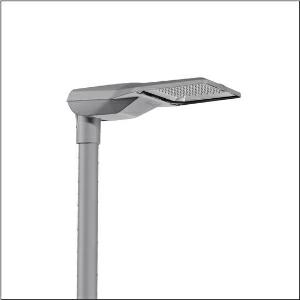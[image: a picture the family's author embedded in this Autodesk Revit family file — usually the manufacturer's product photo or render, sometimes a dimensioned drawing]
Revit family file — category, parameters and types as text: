
# Revit family: streetlight_sl_21_iq_midi___st0_8a_5xe3c61g08nb_b7e9
name_source: partatom
category: Lighting Fixtures
units: mm (PartAtom-declared; Revit-internal decimal feet)

## family parameters
Cut with Voids When Loaded = No
Host = Face
Light Source = No
Part Type = Normal
Room Calculation Point = No
Round Connector Dimension = Use Diameter
Shared = No

## types (1)
- --- (1 x LED, 20820 lm, 155.5 W, 2700K)
    Apparent Load = 155 VA
    CIE Flux Codes = 41 75 97 100 100
    Color Rendering = 70
    Color Temperature = 2700K
    Default Elevation = 1800 mm
    Description = Streetlight SL 21 iQ midi, mast luminaire, primary light control with lens, of PMMA, primary optical cover: cover, of toughened safety glass, transparent, light distribution: ST0.8a, light emission: direct distribution, primary light characteristic: asymmetric, installation type: post-top, side-entry, LED, High Power LED, rated luminous flux: 20.820lm, luminous efficacy: 134lm/W, light colour: 727, colour temperature: 2700K, control: Street-Remote, Auto-Match, Temp-Guard, Lumen-Switch, Night-Set, Smart-Wire, Light-Fading, Desk-Remote (wireless, voltage-free reading and setting of iQ features in the workshop via application-optimized NFC function/RFID function), optimised constant luminous flux control (CLO 2.0), presetting dimming linear, mains connection: 230..240V, AC, 50/60Hz, start of lifetime: 156W, end of service life: 162W, reduction: 69W, luminaire housing, of diecast aluminium, powder-coated, Siteco® metallic grey (DB 702S), corrosivity category C5 mid according to DIN EN ISO 12944, please order mast flange separately, inclination adjustable: 0°, 5°, 10°, 15°, sealing non-destructively replaceable, multi-level sealing system, length: 644mm, width: 335mm, height: 110mm, mast flange for spigot size: 42mm (side-entry): 5XC10008XM4, 60/48mm (side-entry/post-top): 5XC10108XM2, 76/60mm (side-entry/post-top): 5XC10108XM1, protection rating (complete): IP66, insulation class (complete): insulation class II (safety insulation), certification: CE, ENEC, ENEC+, VDE, impact resistance: IK09, permissible operating ambient temperature for outdoor applications: -40..+50°C, standard-compliant lighting for roads and squares, packaging unit: 1 piece

Light Distribution: ST0.8a
    Height = 111 mm
    Lamp = 1 x LED
    Lamp Light Flux = 20820 lm
    Lamp Power = 155.5 W
    Lamp count = 1
    Length = 644 mm
    Luminous efficacy = 134 lm/W
    Manufacturer = Siteco
    ModVariant = No
    Model = 5XE3C61G08NB
    Number of Poles = 1
    OnlyDefault = Yes
    Power Factor = 1
    Product Name = Streetlight SL 21 iQ midi | ST0.8a
    Product group = mast luminaire | pylon top
    ProductGroupID = 6100
    Protection Class = Protection class II
    Protection Degree = IP 66
    RLX_Detail_Level = 1
    RLX_Emergency_Light_Flux = 0 lm
    RLX_Emergency_Type = 0
    RLX_Emergency_Type_DB = No
    RlxData = <blob elided: 91277 chars, md5=0ad41ddc>
    Socket = socket
    Standby Power = 0 W
    System Light Flux = 20820 lm
    System Power = 155 W
    Type Comments = factory setting: luminous flux: 100 % | dim-lin: 254 | 823 mA
    Type Image = l_1004298.jpg
    URL = http://relux.com
    VarID = @adj_101225
    Voltage = 0 V
    Weight = 0.00 kg
    Width = 336 mm

## geometry (parser evidence)
native form markers: Blend x4, Sweep x11
no freeform markers — native parametric forms only
